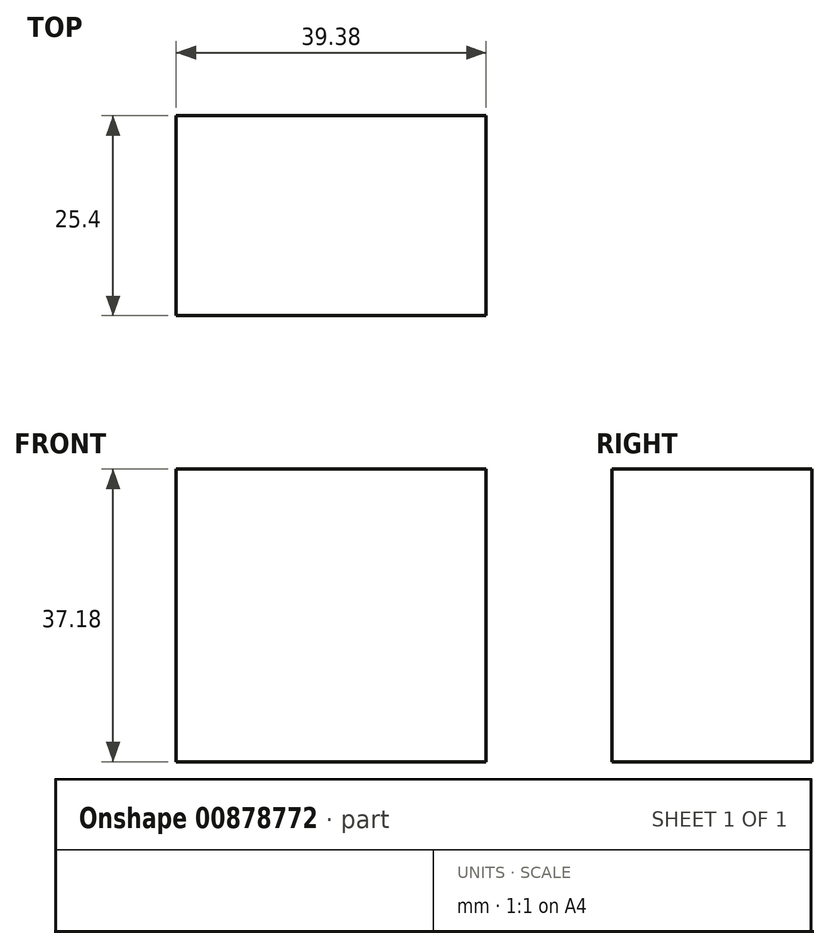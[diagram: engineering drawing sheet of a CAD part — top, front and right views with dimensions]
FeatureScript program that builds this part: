
annotation { "Feature Type Name" : "Feature", "Feature Type Description" : "" }
export const myFeature = defineFeature(function(context is Context, id is Id, definition is map)
    precondition{}
    {
        {
            var Q0;
            Q0=qCreatedBy(makeId("Front.planeOp"),FACE);
            var sketch = newSketch(context, id + "F0", { "sketchPlane" : qUnion([Q0])});
            skLineSegment(sketch, "E0", {"start": v(0, 0) * mm, "end": v(-39.38, 0) * mm});
            skLineSegment(sketch, "E1", {"start": v(-39.38, 0) * mm, "end": v(-39.38, 37.18) * mm});
            skLineSegment(sketch, "E2", {"start": v(-39.38, 37.18) * mm, "end": v(0, 37.18) * mm});
            skLineSegment(sketch, "E3", {"start": v(0, 37.18) * mm, "end": v(0, 0) * mm});
            skSolve(sketch);
        }
        {
            var Q0;
            Q0=makeQuery(id+"F0.imprint","IMPRINT",FACE,{"disambiguationData":[TD([[makeQuery(id+"F0.imprint","IMPRINT",EDGE,{"derivedFrom":sQuery(id+"F0.wireOp",EDGE,"E0")}),-1.0]])]});
            extrude(context, id + "F1", {"entities" : qUnion([Q0]), "depth" : 25.4 * mm, "offsetDistance" : 25.4 * mm});
        }
    });
